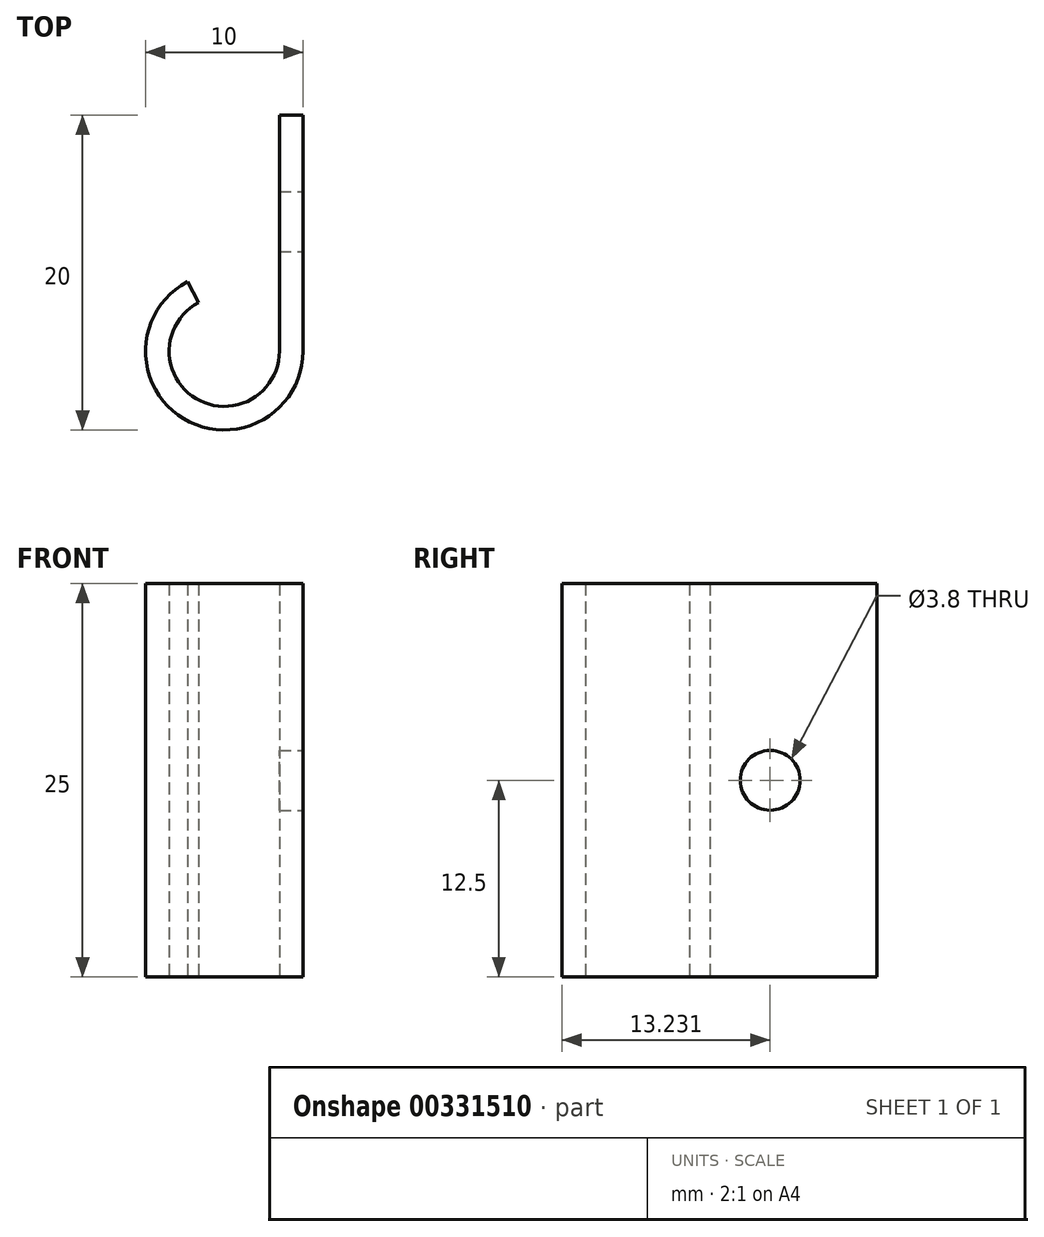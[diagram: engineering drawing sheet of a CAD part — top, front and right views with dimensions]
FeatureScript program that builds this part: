
annotation { "Feature Type Name" : "Feature", "Feature Type Description" : "" }
export const myFeature = defineFeature(function(context is Context, id is Id, definition is map)
    precondition{}
    {
        {
            var Q0;
            Q0=qCreatedBy(makeId("Top.planeOp"),FACE);
            var sketch = newSketch(context, id + "F0", { "sketchPlane" : qUnion([Q0])});
            skArc(sketch, "E0", {"start": v(-1.64, 3.1) * mm, "mid": v(-1.8, -3) * mm, "end": v(3.5, 0) * mm});
            skArc(sketch, "E1", {"start": v(-2.34, 4.42) * mm, "mid": v(-2.58, -4.28) * mm, "end": v(5, 0) * mm});
            skPoint(sketch, "E2", {"position": v(0, 15) * mm});
            skLineSegment(sketch, "E3", {"start": v(0, 15) * mm, "end": v(11.47, 15) * mm, "construction": true});
            skPoint(sketch, "E4", {"position": v(5, 15) * mm});
            skPoint(sketch, "E5", {"position": v(5, 0) * mm});
            skPoint(sketch, "E6", {"position": v(3.5, 0) * mm});
            skLineSegment(sketch, "E7.top", {"start": v(3.5, 15) * mm, "end": v(5, 15) * mm});
            skLineSegment(sketch, "E7.left", {"start": v(3.5, 0) * mm, "end": v(3.5, 15) * mm});
            skLineSegment(sketch, "E7.right", {"start": v(5, 0) * mm, "end": v(5, 15) * mm});
            skPoint(sketch, "E8", {"position": v(0, -5) * mm});
            skLineSegment(sketch, "E9", {"start": v(-1.64, 3.1) * mm, "end": v(-2.34, 4.42) * mm});
            skSolve(sketch);
        }
        {
            var Q0;
            Q0 = qSketchRegion(id + "F0", true);
            extrude(context, id + "F1", {"entities" : qUnion([Q0]), "depth" : 25 * mm, "offsetDistance" : 25 * mm});
        }
        {
            var Q0;
            Q0=makeQuery(id+"F1.opExtrude","SWEPT_FACE",FACE,{"disambiguationData":[OSD([sQuery(id+"F0.wireOp",EDGE,"E7.left")])]});
            var sketch = newSketch(context, id + "F2", { "sketchPlane" : qUnion([Q0])});
            skLineSegment(sketch, "E10", {"start": v(0, 12.5) * mm, "end": v(-19.57, 12.5) * mm, "construction": true});
            skLineSegment(sketch, "E11", {"start": v(-15, 25) * mm, "end": v(-15, 0) * mm, "construction": true});
            skLineSegment(sketch, "E12", {"start": v(-4.37, 25.83) * mm, "end": v(-4.37, -2.02) * mm, "construction": true});
            skPoint(sketch, "E13", {"position": v(-4.37, 12.5) * mm});
            skPoint(sketch, "E14", {"position": v(-8.23, 12.5) * mm});
            skSolve(sketch);
        }
        {
            var Q0;
            Q0=sQuery(id+"F2.wireOp",VERTEX,"E14");
            var Q1;
            Q1=makeQuery(id+"F1.opExtrude","SWEPT_BODY",BODY,{"disambiguationData":[OSD([sQuery(id+"F0.wireOp",EDGE,"E0"),sQuery(id+"F0.wireOp",EDGE,"E1"),sQuery(id+"F0.wireOp",EDGE,"E7.top"),sQuery(id+"F0.wireOp",EDGE,"E7.left"),sQuery(id+"F0.wireOp",EDGE,"E7.right"),sQuery(id+"F0.wireOp",EDGE,"E9")])]});
            hole(context, id + "F3", {"style" : HoleStyle.SIMPLE, "endStyle" : HoleEndStyle.BLIND, "holeDiameter" : 3.8 * mm, "majorDiameter" : 5 * mm, "holeDepth" : 20 * mm, "isTappedThrough" : true, "tappedDepth" : 12 * mm, "tapClearance" : 3, "startFromSketch" : true, "locations" : qUnion([Q0]), "scope" : qUnion([Q1])});
        }
    });
